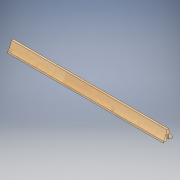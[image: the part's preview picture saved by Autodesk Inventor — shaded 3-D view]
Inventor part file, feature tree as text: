
AUTODESK INVENTOR PART (.ipt)
format: ipt  version: 2022.2 (Build 262287010, 287A)  size: 180,736 bytes
history: native  units: in
note: dims shown in document units (in); Inventor stores cm internally (conversion verified against a paired STEP export)
features: revolve x2, other x1, direct_edit x1
ambient origin geometry x8: Origin, YZ Plane, XZ Plane, XY Plane, X Axis, Y Axis, Z Axis, Center Point
bodies: Solid1 (feature_tree)
feature tree (4):
  other  "Lower Mull (2)"
  direct_edit  "Direct Edit1"
  revolve  "Rotate1"  [1 undecoded]
  revolve  "Rotate2"  Angle=180.0deg
note: 1 required parameter value undecoded (feature->parameter linkage not recoverable at this tier; creation-order binding heuristic only, values carry confidence <= 0.55)
